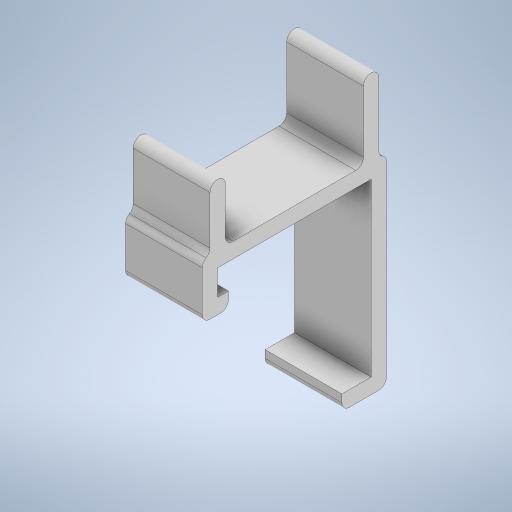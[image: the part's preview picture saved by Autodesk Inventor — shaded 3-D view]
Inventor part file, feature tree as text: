
AUTODESK INVENTOR PART (.ipt)
format: ipt  version: 2023 (Build 270158030, 158C)  size: 293,376 bytes
history: native  units: mm
features: extrude x2, fillet x2, sketch x2
ambient origin geometry x8: Origin, YZ Plane, XZ Plane, XY Plane, X Axis, Y Axis, Z Axis, Center Point
bodies: Solid1 (feature_tree)
feature tree (6):
  extrude  "Extrusion1"  Depth=1.65mm
  fillet  "Fillet1"  Radius=10.0mm
  extrude  "Extrusion2"  Depth=1.0mm
  fillet  "Fillet2"  Radius=1.0mm
  sketch  "Sketch1"  dims[d0=0.7mm d1=1.65mm d2=10.0mm]
  sketch  "Sketch2"  dims[d3=11.165365mm d4=1.0mm d5=1.0mm d6=1.0mm d7=1.0mm d8=1.0mm d9=1.9mm d10=5.0mm d11=0.0mm d12=0.5mm d13=10.0mm d14=1.0mm d15=1.0mm d16=5.0mm d17=4.0mm d18=5.0mm d19=0.0mm d20=0.5mm]
